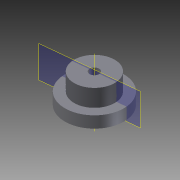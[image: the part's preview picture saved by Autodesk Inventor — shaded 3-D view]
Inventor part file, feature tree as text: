
AUTODESK INVENTOR PART (.ipt)
format: ipt  version: 2012 (Build 160160000, 160)  size: 2,043,904 bytes
history: native  units: mm
features: sketch x7, projected_geometry x5, other x4, extrude x4, plane x1
ambient origin geometry x8: Origin, YZ Plane, XZ Plane, XY Plane, X Axis, Y Axis, Z Axis, Center Point
bodies: Solid1 (feature_tree)
feature tree (21):
  other  "Gear2_LargeAndSmall.iam"
  other  "Spur Gear2:1"
  other  "Spur Gear1:1"
  sketch  "Sketch2"  dims[d0=10.0mm d1=3.3mm]
  sketch  "Sketch3"  dims[d2=10.0mm d3=0.0mm d4=0.0mm d5=0.0mm]
  other  "Work Axis1"
  extrude  "Extrusion1"  Depth=3.3mm
  sketch  "Sketch5"
  plane  "Work Plane1"
  extrude  "Extrusion2"  TaperAngle=0.0deg  [1 undecoded]
  extrude  "Extrusion3"  Depth=10.0mm TaperAngle=0.0deg
  extrude  "Extrusion4"  [1 undecoded]
  projected_geometry  "Projected Loop1"
  projected_geometry  "Projected Loop2"
  sketch  "Sketch4"  dims[d6=0.0mm d7=0.0mm d8=10.0mm d9=0.0mm]
  sketch  "Sketch6"
  projected_geometry  "Projected Loop3"
  sketch  "Sketch7"
  projected_geometry  "Projected Loop4"
  sketch  "Sketch8"
  projected_geometry  "Projected Loop6"
note: 2 required parameter values undecoded (feature->parameter linkage not recoverable at this tier; creation-order binding heuristic only, values carry confidence <= 0.55)
